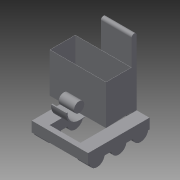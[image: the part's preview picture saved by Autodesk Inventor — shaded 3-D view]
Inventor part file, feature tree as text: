
AUTODESK INVENTOR PART (.ipt)
format: ipt  version: 2015 SP2 (Build 190223200, 223)  size: 221,184 bytes
history: native  units: in
note: dims shown in document units (in); Inventor stores cm internally (conversion verified against a paired STEP export)
features: extrude x7, sketch x7, shell x1, plane x1
ambient origin geometry x8: Origin, YZ Plane, XZ Plane, XY Plane, X Axis, Y Axis, Z Axis, Center Point
bodies: Solid1 (feature_tree)
feature tree (16):
  extrude  "Extrusion1"  Depth=22.0in
  extrude  "Extrusion2"  Depth=6.0in
  extrude  "Extrusion3"  Depth=6.0in
  extrude  "Extrusion4"  Depth=3.5in
  extrude  "Extrusion5"  Depth=12.0in
  extrude  "Extrusion6"  Depth=4.0in
  shell  "Shell1"  Thickness=4.0in
  plane  "Work Plane1"
  extrude  "Extrusion7"  Depth=5.0in
  sketch  "Sketch1"  dims[d0=24.0in d1=22.0in]
  sketch  "Sketch2"  dims[d2=4.0in d3=0.0in d4=6.0in]
  sketch  "Sketch3"  dims[d5=6.0in d6=6.0in]
  sketch  "Sketch4"  dims[d7=3.5in d8=3.5in]
  sketch  "Sketch5"  dims[d9=3.5in d10=12.0in]
  sketch  "Sketch7"  dims[d11=3.5in d12=3.5in d13=4.0in d14=0.0in]
  sketch  "Sketch8"  dims[d15=2.0in d16=5.0in d17=5.0in d18=0.0in d19=4.0in d20=0.0in d21=4.0in d22=0.0in d23=2.0in d24=5.0in d26=2.0in d27=32.0in d28=4.0in d29=0.0in d30=5.0in d31=20.5in d32=15.0in d33=0.5978in d34=10.0in d35=5.0in d36=26.0in d37=4.0in d38=0.0in d39=0.1in d40=9.0in d41=4.0in d42=10.0in d43=0.0344in d44=6.0in d45=0.0in]
